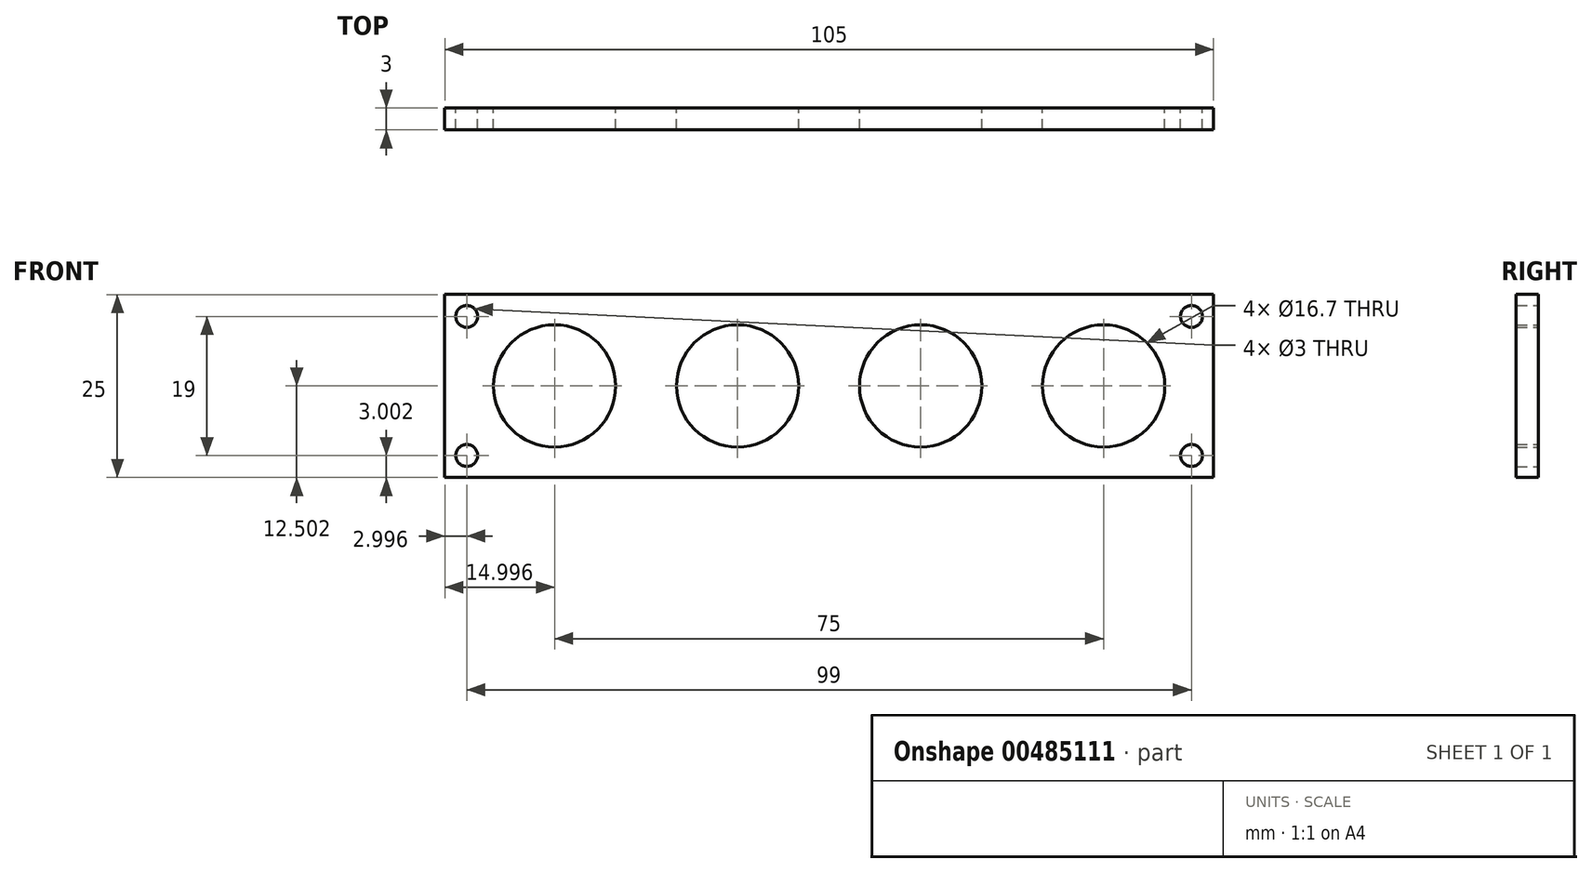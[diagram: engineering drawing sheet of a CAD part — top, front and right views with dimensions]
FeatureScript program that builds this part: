
annotation { "Feature Type Name" : "Feature", "Feature Type Description" : "" }
export const myFeature = defineFeature(function(context is Context, id is Id, definition is map)
    precondition{}
    {
        {
            var Q0;
            Q0=qCreatedBy(makeId("Front.planeOp"),FACE);
            var sketch = newSketch(context, id + "F0", { "sketchPlane" : qUnion([Q0])});
            skLineSegment(sketch, "E0.bottom", {"start": v(-48.3, 6.84) * mm, "end": v(56.7, 6.84) * mm, "construction": true});
            skLineSegment(sketch, "E0.top", {"start": v(-48.3, -5.66) * mm, "end": v(56.7, -5.66) * mm});
            skLineSegment(sketch, "E0.left", {"start": v(-48.3, 6.84) * mm, "end": v(-48.3, -5.66) * mm});
            skLineSegment(sketch, "E0.right", {"start": v(56.7, 6.84) * mm, "end": v(56.7, -5.66) * mm});
            skLineSegment(sketch, "E1", {"start": v(-33.3, 6.84) * mm, "end": v(-33.3, -5.66) * mm, "construction": true});
            skLineSegment(sketch, "E2", {"start": v(-8.3, 6.84) * mm, "end": v(-8.3, -5.66) * mm, "construction": true});
            skLineSegment(sketch, "E3", {"start": v(16.7, 6.84) * mm, "end": v(16.7, -5.66) * mm, "construction": true});
            skCircle(sketch, "E4", {"center": v(-33.3, 6.84) * mm, "radius": 8.35 * mm});
            skCircle(sketch, "E5", {"center": v(-8.3, 6.84) * mm, "radius": 8.35 * mm});
            skCircle(sketch, "E6", {"center": v(16.7, 6.84) * mm, "radius": 8.35 * mm});
            skLineSegment(sketch, "E7", {"start": v(41.7, 6.84) * mm, "end": v(41.7, -5.66) * mm, "construction": true});
            skCircle(sketch, "E8", {"center": v(41.7, 6.84) * mm, "radius": 8.35 * mm});
            skLineSegment(sketch, "E9.top", {"start": v(-48.3, 19.34) * mm, "end": v(56.7, 19.34) * mm});
            skLineSegment(sketch, "E9.left", {"start": v(-48.3, 6.84) * mm, "end": v(-48.3, 19.34) * mm});
            skLineSegment(sketch, "E9.right", {"start": v(56.7, 6.84) * mm, "end": v(56.7, 19.34) * mm});
            skLineSegment(sketch, "E10", {"start": v(-45.3, 19.34) * mm, "end": v(-45.3, -5.66) * mm, "construction": true});
            skLineSegment(sketch, "E11", {"start": v(53.7, 19.34) * mm, "end": v(53.7, -5.66) * mm, "construction": true});
            skLineSegment(sketch, "E12", {"start": v(-48.3, -2.66) * mm, "end": v(56.7, -2.66) * mm, "construction": true});
            skLineSegment(sketch, "E13", {"start": v(-48.3, 16.34) * mm, "end": v(56.7, 16.34) * mm, "construction": true});
            skCircle(sketch, "E14", {"center": v(-45.3, 16.34) * mm, "radius": 1.5 * mm});
            skCircle(sketch, "E15", {"center": v(-45.3, -2.66) * mm, "radius": 1.5 * mm});
            skCircle(sketch, "E16", {"center": v(53.7, 16.34) * mm, "radius": 1.5 * mm});
            skCircle(sketch, "E17", {"center": v(53.7, -2.66) * mm, "radius": 1.5 * mm});
            skSolve(sketch);
        }
        {
            var Q0;
            Q0=makeQuery(id+"F0.imprint","IMPRINT",FACE,{"disambiguationData":[TD([[makeQuery(id+"F0.imprint","IMPRINT",EDGE,{"derivedFrom":sQuery(id+"F0.wireOp",EDGE,"E0.top")}),1.0]])]});
            extrude(context, id + "F1", {"entities" : qUnion([Q0]), "depth" : 3 * mm, "offsetDistance" : 25 * mm});
        }
    });
